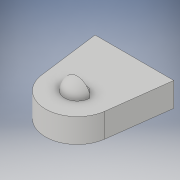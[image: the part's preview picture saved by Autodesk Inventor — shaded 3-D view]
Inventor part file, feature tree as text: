
AUTODESK INVENTOR PART (.ipt)
format: ipt  version: 2019 (Build 230136000, 136)  size: 149,504 bytes
history: native  units: mm
features: sketch x3, hole x2, extrude x1, revolve x1, fillet x1, projected_geometry x1
ambient origin geometry x8: Origin, YZ Plane, XZ Plane, XY Plane, X Axis, Y Axis, Z Axis, Center Point
bodies: Volumenkörper1 (feature_tree)
feature tree (9):
  sketch  "Skizze1"  dims[d0=25.0mm d1=32.0mm]
  extrude  "Extrusion1"  Depth=32.0mm
  hole  "Bohrung1"  [1 undecoded]
  revolve  "Umdrehung1"
  fillet  "Rundung1"  Radius=9.5mm
  hole  "Bohrung2"  [1 undecoded]
  sketch  "Skizze2"  dims[d2=39.0mm d3=35.0mm d4=9.5mm d5=0.0mm]
  sketch  "Skizze3"  dims[d6=10.0mm d7=180.0deg d8=4.0mm d9=6.0mm d10=6.0mm d11=9.0mm d12=90.0deg d13=8.0mm d14=0.0mm d15=1.5mm d16=3.0mm d17=6.0mm d18=6.0mm d19=7.0mm d20=90.0deg d21=8.0mm d22=0.0mm]
  projected_geometry  "Projizierte Kontur1"
note: 2 required parameter values undecoded (feature->parameter linkage not recoverable at this tier; creation-order binding heuristic only, values carry confidence <= 0.55)
